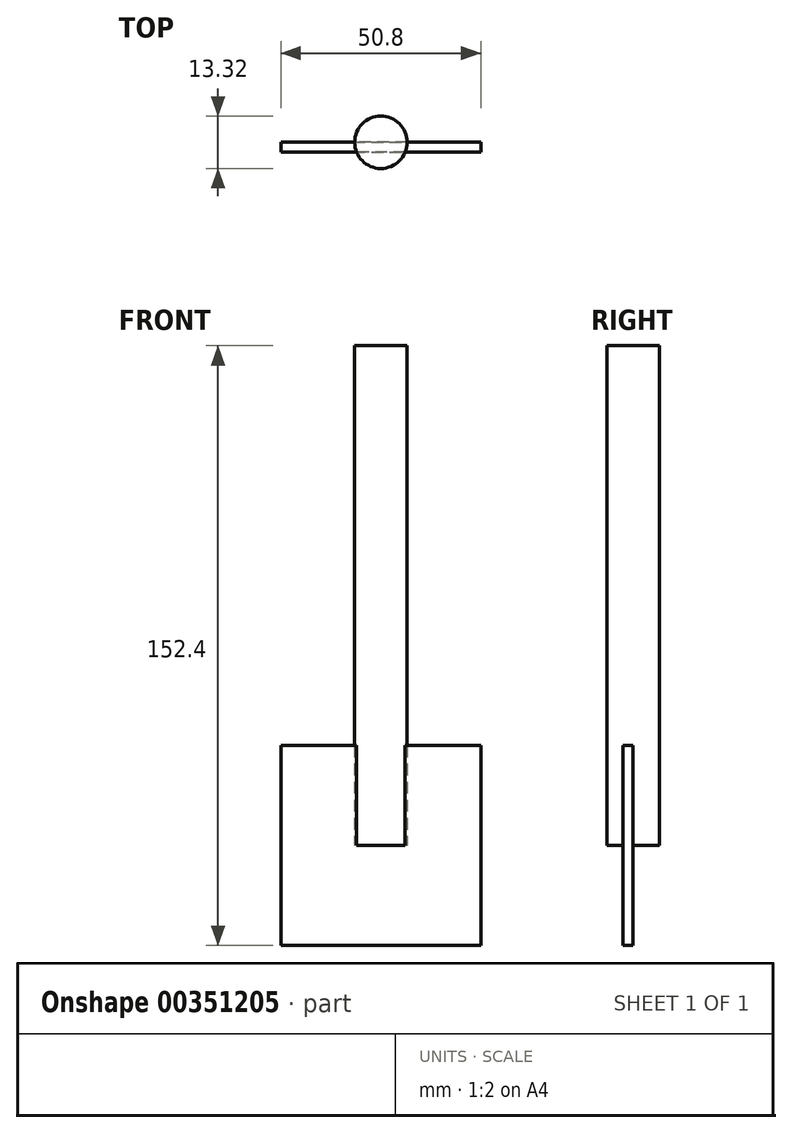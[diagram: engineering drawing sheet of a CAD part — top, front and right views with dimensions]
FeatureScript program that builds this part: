
annotation { "Feature Type Name" : "Feature", "Feature Type Description" : "" }
export const myFeature = defineFeature(function(context is Context, id is Id, definition is map)
    precondition{}
    {
        {
            var Q0;
            Q0=qCreatedBy(makeId("Front.planeOp"),FACE);
            var sketch = newSketch(context, id + "F0", { "sketchPlane" : qUnion([Q0])});
            skLineSegment(sketch, "E0.bottom", {"start": v(-25.4, 25.4) * mm, "end": v(25.4, 25.4) * mm});
            skLineSegment(sketch, "E0.top", {"start": v(-25.4, -25.4) * mm, "end": v(25.4, -25.4) * mm});
            skLineSegment(sketch, "E0.left", {"start": v(-25.4, 25.4) * mm, "end": v(-25.4, -25.4) * mm});
            skLineSegment(sketch, "E0.right", {"start": v(25.4, 25.4) * mm, "end": v(25.4, -25.4) * mm});
            skPoint(sketch, "E0.middle", {"position": v(0, 0) * mm});
            skSolve(sketch);
        }
        {
            var Q0;
            Q0=makeQuery(id+"F0.imprint","IMPRINT",FACE,{"disambiguationData":[TD([[makeQuery(id+"F0.imprint","IMPRINT",EDGE,{"derivedFrom":sQuery(id+"F0.wireOp",EDGE,"E0.bottom")}),-1.0]])]});
            extrude(context, id + "F1", {"entities" : qUnion([Q0]), "depth" : 2.54 * mm});
        }
        {
            var Q0;
            Q0=qCreatedBy(makeId("Top.planeOp"),FACE);
            var sketch = newSketch(context, id + "F2", { "sketchPlane" : qUnion([Q0])});
            skCircle(sketch, "E1", {"center": v(0, 0) * mm, "radius": 6.66 * mm});
            skSolve(sketch);
        }
        {
            var Q0;
            Q0=makeQuery(id+"F2.imprint","IMPRINT",FACE,{"disambiguationData":[TD([[makeQuery(id+"F2.imprint","IMPRINT",EDGE,{"derivedFrom":sQuery(id+"F2.wireOp",EDGE,"E1")}),1.0]])]});
            extrude(context, id + "F3", {"entities" : qUnion([Q0]), "operationType" : NewBodyOperationType.ADD, "depth" : 127 * mm});
        }
    });
